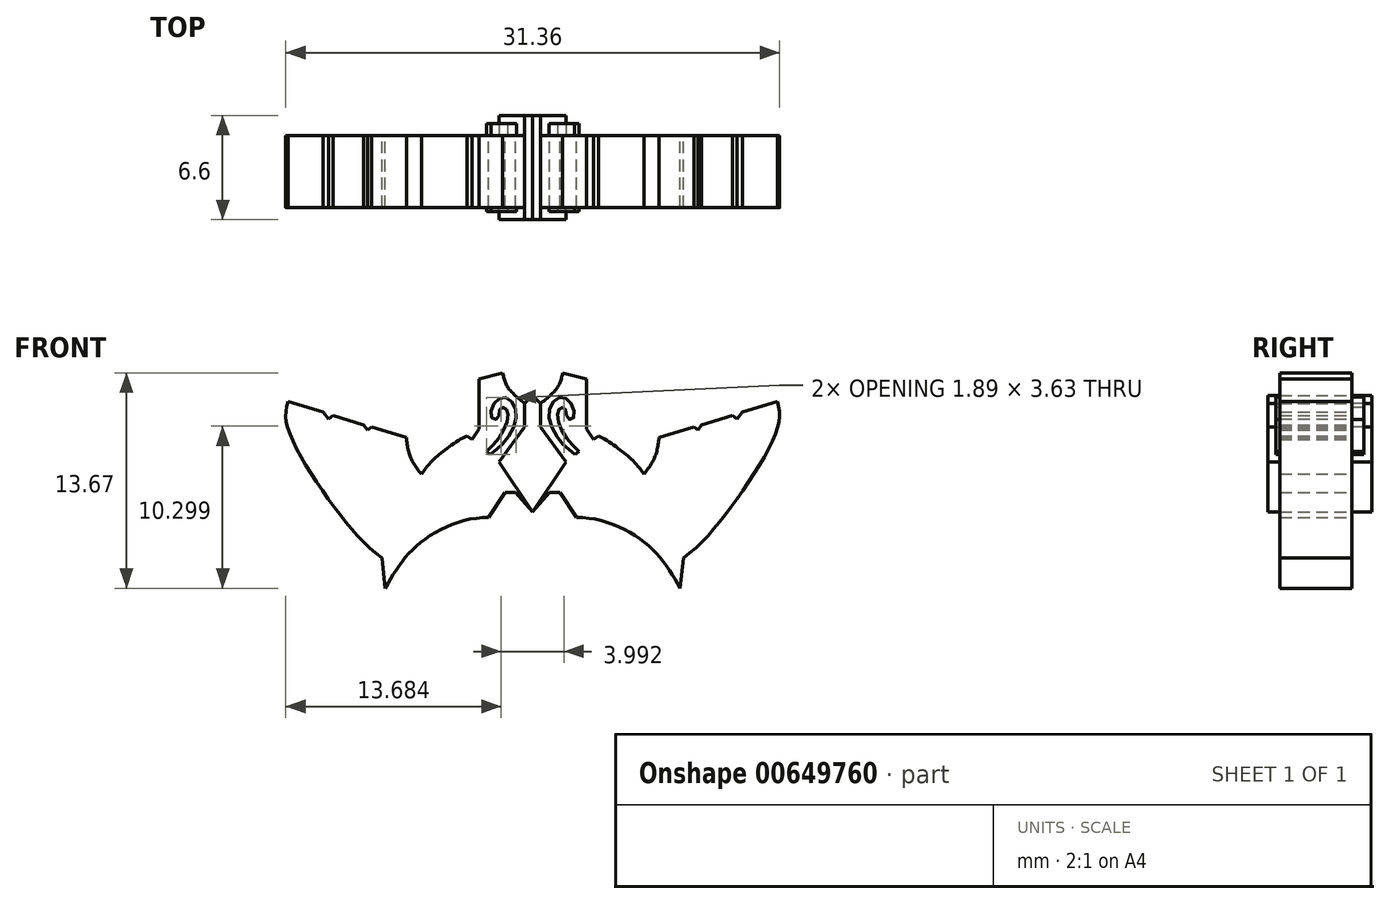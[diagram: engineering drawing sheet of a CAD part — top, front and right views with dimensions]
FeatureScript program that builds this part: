
annotation { "Feature Type Name" : "Feature", "Feature Type Description" : "" }
export const myFeature = defineFeature(function(context is Context, id is Id, definition is map)
    precondition{}
    {
        {
            var Q0;
            Q0=qCreatedBy(makeId("Front.planeOp"),FACE);
            var sketch = newSketch(context, id + "F0", { "sketchPlane" : qUnion([Q0])});
            skLineSegment(sketch, "E0", {"start": v(0, -28.32) * mm, "end": v(-0.51, -28.81) * mm});
            skFitSpline(sketch, "E1", {"points": [v(-0.51, -28.81) * mm, v(-1.6, -27.77) * mm, v(-1.9, -26.9) * mm], "startDerivative": vector(-2.3, 1.83) * mm, "endDerivative": vector(-0.4, 2.02) * mm});
            skLineSegment(sketch, "E2", {"start": v(-1.9, -26.9) * mm, "end": v(-3.41, -27.26) * mm});
            skLineSegment(sketch, "E3", {"start": v(-3.41, -27.26) * mm, "end": v(-3.41, -30.44) * mm});
            skLineSegment(sketch, "E4", {"start": v(-3.41, -30.44) * mm, "end": v(-3.86, -31.1) * mm});
            skLineSegment(sketch, "E5", {"start": v(-3.86, -31.1) * mm, "end": v(-4.17, -30.89) * mm});
            skFitSpline(sketch, "E6", {"points": [v(-4.17, -30.89) * mm, v(-5.74, -31.9) * mm, v(-7.06, -33.32) * mm], "startDerivative": vector(-2.94, -1.25) * mm, "endDerivative": vector(-3.05, -4.45) * mm});
            skFitSpline(sketch, "E7", {"points": [v(-7.06, -33.32) * mm, v(-7.77, -32.2) * mm, v(-8.02, -30.97) * mm], "startDerivative": vector(-1.62, 2.12) * mm, "endDerivative": vector(-0.3, 2.58) * mm});
            skLineSegment(sketch, "E8", {"start": v(-8.02, -30.97) * mm, "end": v(-10.24, -30.3) * mm});
            skLineSegment(sketch, "E9", {"start": v(-10.24, -30.3) * mm, "end": v(-10.5, -30.5) * mm});
            skLineSegment(sketch, "E10", {"start": v(-10.5, -30.5) * mm, "end": v(-10.73, -30.19) * mm});
            skLineSegment(sketch, "E11", {"start": v(-10.73, -30.19) * mm, "end": v(-12.7, -29.6) * mm});
            skLineSegment(sketch, "E12", {"start": v(-12.7, -29.6) * mm, "end": v(-12.97, -29.82) * mm});
            skLineSegment(sketch, "E13", {"start": v(-12.97, -29.82) * mm, "end": v(-13.32, -29.37) * mm});
            skLineSegment(sketch, "E14", {"start": v(-13.32, -29.37) * mm, "end": v(-15.54, -28.7) * mm});
            skFitSpline(sketch, "E15", {"points": [v(-15.54, -28.7) * mm, v(-15.54, -30.43) * mm, v(-12.88, -35.02) * mm, v(-9.57, -38.63) * mm], "startDerivative": vector(-2.17, -7.38) * mm, "endDerivative": vector(9.36, -6.6) * mm});
            skLineSegment(sketch, "E16", {"start": v(-9.57, -38.63) * mm, "end": v(-9.36, -40.56) * mm});
            skFitSpline(sketch, "E17", {"points": [v(-9.36, -40.56) * mm, v(-7.19, -37.7) * mm, v(-2.79, -36.08) * mm], "startDerivative": vector(3.82, 6.79) * mm, "endDerivative": vector(8.98, -0.25) * mm});
            skLineSegment(sketch, "E18", {"start": v(-2.79, -36.08) * mm, "end": v(-1.75, -34.48) * mm});
            skLineSegment(sketch, "E19", {"start": v(-1.75, -34.48) * mm, "end": v(-1.08, -34.48) * mm});
            skLineSegment(sketch, "E20", {"start": v(-1.08, -34.48) * mm, "end": v(0, -35.7) * mm});
            skLineSegment(sketch, "E21.MirrorCS", {"start": v(1.08, -34.48) * mm, "end": v(0, -35.7) * mm});
            skLineSegment(sketch, "E22.MirrorCS", {"start": v(1.75, -34.48) * mm, "end": v(1.08, -34.48) * mm});
            skLineSegment(sketch, "E23.MirrorCS", {"start": v(2.79, -36.08) * mm, "end": v(1.75, -34.48) * mm});
            skFitSpline(sketch, "E24.MirrorCS", {"points": [v(9.36, -40.56) * mm, v(7.19, -37.7) * mm, v(2.79, -36.08) * mm], "startDerivative": vector(-3.82, 6.79) * mm, "endDerivative": vector(-8.98, -0.25) * mm});
            skLineSegment(sketch, "E25.MirrorCS", {"start": v(9.57, -38.63) * mm, "end": v(9.36, -40.56) * mm});
            skFitSpline(sketch, "E26.MirrorCS", {"points": [v(15.54, -28.7) * mm, v(15.54, -30.43) * mm, v(12.88, -35.02) * mm, v(9.57, -38.63) * mm], "startDerivative": vector(2.17, -7.38) * mm, "endDerivative": vector(-9.36, -6.6) * mm});
            skLineSegment(sketch, "E27.MirrorCS", {"start": v(13.32, -29.37) * mm, "end": v(15.54, -28.7) * mm});
            skLineSegment(sketch, "E28.MirrorCS", {"start": v(12.97, -29.82) * mm, "end": v(13.32, -29.37) * mm});
            skLineSegment(sketch, "E29.MirrorCS", {"start": v(12.7, -29.6) * mm, "end": v(12.97, -29.82) * mm});
            skLineSegment(sketch, "E30.MirrorCS", {"start": v(10.73, -30.19) * mm, "end": v(12.7, -29.6) * mm});
            skLineSegment(sketch, "E31.MirrorCS", {"start": v(10.5, -30.5) * mm, "end": v(10.73, -30.19) * mm});
            skLineSegment(sketch, "E32.MirrorCS", {"start": v(10.24, -30.3) * mm, "end": v(10.5, -30.5) * mm});
            skLineSegment(sketch, "E33.MirrorCS", {"start": v(8.02, -30.97) * mm, "end": v(10.24, -30.3) * mm});
            skFitSpline(sketch, "E34.MirrorCS", {"points": [v(7.06, -33.32) * mm, v(7.77, -32.2) * mm, v(8.02, -30.97) * mm], "startDerivative": vector(1.62, 2.12) * mm, "endDerivative": vector(0.3, 2.58) * mm});
            skFitSpline(sketch, "E35.MirrorCS", {"points": [v(4.17, -30.89) * mm, v(5.74, -31.9) * mm, v(7.06, -33.32) * mm], "startDerivative": vector(2.94, -1.25) * mm, "endDerivative": vector(3.05, -4.45) * mm});
            skLineSegment(sketch, "E36.MirrorCS", {"start": v(3.86, -31.1) * mm, "end": v(4.17, -30.89) * mm});
            skLineSegment(sketch, "E37.MirrorCS", {"start": v(3.41, -30.44) * mm, "end": v(3.86, -31.1) * mm});
            skLineSegment(sketch, "E38.MirrorCS", {"start": v(3.41, -27.26) * mm, "end": v(3.41, -30.44) * mm});
            skLineSegment(sketch, "E39.MirrorCS", {"start": v(1.9, -26.9) * mm, "end": v(3.41, -27.26) * mm});
            skFitSpline(sketch, "E40.MirrorCS", {"points": [v(0.51, -28.81) * mm, v(1.6, -27.77) * mm, v(1.9, -26.9) * mm], "startDerivative": vector(2.3, 1.83) * mm, "endDerivative": vector(0.4, 2.02) * mm});
            skLineSegment(sketch, "E41.MirrorCS", {"start": v(0, -28.32) * mm, "end": v(0.51, -28.81) * mm});
            skSolve(sketch);
        }
        {
            var Q0;
            Q0=makeQuery(id+"F0.imprint","IMPRINT",FACE,{"disambiguationData":[TD([[makeQuery(id+"F0.imprint","IMPRINT",EDGE,{"derivedFrom":sQuery(id+"F0.wireOp",EDGE,"E0")}),1.0]])]});
            extrude(context, id + "F1", {"entities" : qUnion([Q0]), "depth" : 4.57 * mm, "offsetDistance" : 25.4 * mm});
        }
        {
            var Q0;
            Q0=makeQuery(id+"F1.opExtrude","CAP_FACE",FACE,{"disambiguationData":[OSD([sQuery(id+"F0.wireOp",EDGE,"E0"),sQuery(id+"F0.wireOp",EDGE,"E1"),sQuery(id+"F0.wireOp",EDGE,"E2"),sQuery(id+"F0.wireOp",EDGE,"E3"),sQuery(id+"F0.wireOp",EDGE,"E4"),sQuery(id+"F0.wireOp",EDGE,"E5"),sQuery(id+"F0.wireOp",EDGE,"E6"),sQuery(id+"F0.wireOp",EDGE,"E7"),sQuery(id+"F0.wireOp",EDGE,"E8"),sQuery(id+"F0.wireOp",EDGE,"E9"),sQuery(id+"F0.wireOp",EDGE,"E10"),sQuery(id+"F0.wireOp",EDGE,"E11"),sQuery(id+"F0.wireOp",EDGE,"E12"),sQuery(id+"F0.wireOp",EDGE,"E13"),sQuery(id+"F0.wireOp",EDGE,"E14"),sQuery(id+"F0.wireOp",EDGE,"E15"),sQuery(id+"F0.wireOp",EDGE,"E16"),sQuery(id+"F0.wireOp",EDGE,"E17"),sQuery(id+"F0.wireOp",EDGE,"E18"),sQuery(id+"F0.wireOp",EDGE,"E19"),sQuery(id+"F0.wireOp",EDGE,"E20"),sQuery(id+"F0.wireOp",EDGE,"E21.MirrorCS"),sQuery(id+"F0.wireOp",EDGE,"E22.MirrorCS"),sQuery(id+"F0.wireOp",EDGE,"E23.MirrorCS"),sQuery(id+"F0.wireOp",EDGE,"E24.MirrorCS"),sQuery(id+"F0.wireOp",EDGE,"E25.MirrorCS"),sQuery(id+"F0.wireOp",EDGE,"E26.MirrorCS"),sQuery(id+"F0.wireOp",EDGE,"E27.MirrorCS"),sQuery(id+"F0.wireOp",EDGE,"E28.MirrorCS"),sQuery(id+"F0.wireOp",EDGE,"E29.MirrorCS"),sQuery(id+"F0.wireOp",EDGE,"E30.MirrorCS"),sQuery(id+"F0.wireOp",EDGE,"E31.MirrorCS"),sQuery(id+"F0.wireOp",EDGE,"E32.MirrorCS"),sQuery(id+"F0.wireOp",EDGE,"E33.MirrorCS"),sQuery(id+"F0.wireOp",EDGE,"E34.MirrorCS"),sQuery(id+"F0.wireOp",EDGE,"E35.MirrorCS"),sQuery(id+"F0.wireOp",EDGE,"E36.MirrorCS"),sQuery(id+"F0.wireOp",EDGE,"E37.MirrorCS"),sQuery(id+"F0.wireOp",EDGE,"E38.MirrorCS"),sQuery(id+"F0.wireOp",EDGE,"E39.MirrorCS"),sQuery(id+"F0.wireOp",EDGE,"E40.MirrorCS"),sQuery(id+"F0.wireOp",EDGE,"E41.MirrorCS")])],"isStart":false});
            var sketch = newSketch(context, id + "F2", { "sketchPlane" : qUnion([Q0])});
            skLineSegment(sketch, "E42", {"start": v(0.51, -28.81) * mm, "end": v(0.51, -30.32) * mm});
            skLineSegment(sketch, "E43", {"start": v(0.51, -30.32) * mm, "end": v(2.13, -32.55) * mm});
            skLineSegment(sketch, "E44", {"start": v(2.13, -32.55) * mm, "end": v(0, -35.7) * mm});
            skLineSegment(sketch, "E45.MirrorCS", {"start": v(-0.51, -28.81) * mm, "end": v(-0.51, -30.32) * mm});
            skLineSegment(sketch, "E46.MirrorCS", {"start": v(-0.51, -30.32) * mm, "end": v(-2.13, -32.55) * mm});
            skLineSegment(sketch, "E47.MirrorCS", {"start": v(-2.13, -32.55) * mm, "end": v(0, -35.7) * mm});
            skLineSegment(sketch, "E48", {"start": v(-0.51, -28.81) * mm, "end": v(0, -28.32) * mm});
            skLineSegment(sketch, "E49", {"start": v(0, -28.32) * mm, "end": v(0.51, -28.81) * mm});
            skSolve(sketch);
        }
        {
            var Q0;
            Q0=makeQuery(id+"F2.imprint","IMPRINT",FACE,{"disambiguationData":[TD([[makeQuery(id+"F2.imprint","IMPRINT",EDGE,{"derivedFrom":sQuery(id+"F2.wireOp",EDGE,"E42")}),-1.0]])]});
            extrude(context, id + "F3", {"entities" : qUnion([Q0]), "operationType" : NewBodyOperationType.ADD, "depth" : 0.76 * mm, "offsetDistance" : 25.4 * mm});
        }
        {
            var Q0;
            {var subQ0=sQuery(id+"F0.wireOp",EDGE,"E40.MirrorCS");var subQ1=sQuery(id+"F0.wireOp",EDGE,"E39.MirrorCS");var subQ2=sQuery(id+"F0.wireOp",EDGE,"E38.MirrorCS");var subQ3=sQuery(id+"F0.wireOp",EDGE,"E37.MirrorCS");var subQ4=sQuery(id+"F0.wireOp",EDGE,"E36.MirrorCS");var subQ5=sQuery(id+"F0.wireOp",EDGE,"E35.MirrorCS");var subQ6=sQuery(id+"F0.wireOp",EDGE,"E34.MirrorCS");var subQ7=sQuery(id+"F0.wireOp",EDGE,"E33.MirrorCS");var subQ8=sQuery(id+"F0.wireOp",EDGE,"E32.MirrorCS");var subQ9=sQuery(id+"F0.wireOp",EDGE,"E31.MirrorCS");var subQ10=sQuery(id+"F0.wireOp",EDGE,"E30.MirrorCS");var subQ11=sQuery(id+"F0.wireOp",EDGE,"E29.MirrorCS");var subQ12=sQuery(id+"F0.wireOp",EDGE,"E22.MirrorCS");var subQ13=sQuery(id+"F0.wireOp",EDGE,"E21.MirrorCS");var subQ14=sQuery(id+"F0.wireOp",EDGE,"E20");var subQ15=sQuery(id+"F0.wireOp",EDGE,"E41.MirrorCS");var subQ16=sQuery(id+"F0.wireOp",EDGE,"E28.MirrorCS");var subQ17=sQuery(id+"F0.wireOp",EDGE,"E27.MirrorCS");var subQ18=sQuery(id+"F0.wireOp",EDGE,"E26.MirrorCS");var subQ19=sQuery(id+"F0.wireOp",EDGE,"E25.MirrorCS");var subQ20=sQuery(id+"F0.wireOp",EDGE,"E24.MirrorCS");var subQ21=sQuery(id+"F0.wireOp",EDGE,"E23.MirrorCS");var subQ22=makeQuery(id+"F1.opExtrude","CAP_FACE",FACE,{"disambiguationData":[OSD([sQuery(id+"F0.wireOp",EDGE,"E0"),sQuery(id+"F0.wireOp",EDGE,"E1"),sQuery(id+"F0.wireOp",EDGE,"E2"),sQuery(id+"F0.wireOp",EDGE,"E3"),sQuery(id+"F0.wireOp",EDGE,"E4"),sQuery(id+"F0.wireOp",EDGE,"E5"),sQuery(id+"F0.wireOp",EDGE,"E6"),sQuery(id+"F0.wireOp",EDGE,"E7"),sQuery(id+"F0.wireOp",EDGE,"E8"),sQuery(id+"F0.wireOp",EDGE,"E9"),sQuery(id+"F0.wireOp",EDGE,"E10"),sQuery(id+"F0.wireOp",EDGE,"E11"),sQuery(id+"F0.wireOp",EDGE,"E12"),sQuery(id+"F0.wireOp",EDGE,"E13"),sQuery(id+"F0.wireOp",EDGE,"E14"),sQuery(id+"F0.wireOp",EDGE,"E15"),sQuery(id+"F0.wireOp",EDGE,"E16"),sQuery(id+"F0.wireOp",EDGE,"E17"),sQuery(id+"F0.wireOp",EDGE,"E18"),sQuery(id+"F0.wireOp",EDGE,"E19"),subQ14,subQ13,subQ12,subQ21,subQ20,subQ19,subQ18,subQ17,subQ16,subQ11,subQ10,subQ9,subQ8,subQ7,subQ6,subQ5,subQ4,subQ3,subQ2,subQ1,subQ0,subQ15])],"isStart":false});Q0=makeQuery(id+"F3.boolean.opBoolean","SPLIT",FACE,{"disambiguationData":[TD([makeQuery(id+"F1.opExtrude","SWEPT_FACE",FACE,{"disambiguationData":[OSD([subQ12])]})])],"derivedFrom":subQ22});}
            var sketch = newSketch(context, id + "F4", { "sketchPlane" : qUnion([Q0])});
            skLineSegment(sketch, "E50", {"start": v(3.86, -31.1) * mm, "end": v(2.13, -32.55) * mm});
            skFitSpline(sketch, "E51", {"points": [v(2.7, -32.08) * mm, v(1.69, -31.14) * mm, v(1.04, -29.4) * mm, v(1.69, -28.45) * mm, v(2.43, -28.81) * mm, v(2.59, -29.75) * mm, v(2.2, -29.76) * mm, v(2.08, -29.16) * mm, v(1.8, -29.1) * mm, v(1.59, -29.44) * mm, v(1.89, -30.62) * mm, v(2.94, -31.88) * mm], "startDerivative": vector(-9.27, 7) * mm, "endDerivative": vector(9.7, -9.61) * mm});
            skFitSpline(sketch, "E52.MirrorCS", {"points": [v(-2.7, -32.08) * mm, v(-1.69, -31.14) * mm, v(-1.04, -29.4) * mm, v(-1.69, -28.45) * mm, v(-2.43, -28.81) * mm, v(-2.59, -29.75) * mm, v(-2.2, -29.76) * mm, v(-2.08, -29.16) * mm, v(-1.8, -29.1) * mm, v(-1.59, -29.44) * mm, v(-1.89, -30.62) * mm, v(-2.94, -31.88) * mm], "startDerivative": vector(9.27, 7) * mm, "endDerivative": vector(-9.7, -9.61) * mm});
            skLineSegment(sketch, "E53.MirrorCS", {"start": v(-3.86, -31.1) * mm, "end": v(-2.13, -32.55) * mm});
            skSolve(sketch);
        }
        {
            var Q0;
            {var subQ0=sQuery(id+"F4.wireOp",EDGE,"E52.MirrorCS");Q0=makeQuery(id+"F4.imprint","IMPRINT",FACE,{"disambiguationData":[TD([[makeQuery(id+"F4.imprint","IMPRINT",EDGE,{"derivedFrom":subQ0}),1.0]])]});}
            var Q1;
            {var subQ0=sQuery(id+"F4.wireOp",EDGE,"E51");Q1=makeQuery(id+"F4.imprint","IMPRINT",FACE,{"disambiguationData":[TD([[makeQuery(id+"F4.imprint","IMPRINT",EDGE,{"derivedFrom":subQ0}),-1.0]])]});}
            extrude(context, id + "F5", {"entities" : qUnion([Q0, Q1]), "operationType" : NewBodyOperationType.ADD, "depth" : 0.25 * mm, "offsetDistance" : 25.4 * mm});
        }
        {
            var Q0;
            Q0 = qSketchRegion(id + "F2", true);
            extrude(context, id + "F6", {"entities" : qUnion([Q0]), "operationType" : NewBodyOperationType.ADD, "oppositeDirection" : true, "depth" : 5.84 * mm, "offsetDistance" : 25.4 * mm});
        }
        {
            var Q0;
            Q0=makeQuery(id+"F5.opExtrude","CAP_FACE",FACE,{"disambiguationData":[OSD([sQuery(id+"F4.wireOp",EDGE,"E50"),sQuery(id+"F4.wireOp",EDGE,"E51")])],"isStart":false});
            var Q1;
            Q1=makeQuery(id+"F5.opExtrude","CAP_FACE",FACE,{"disambiguationData":[OSD([sQuery(id+"F4.wireOp",EDGE,"E52.MirrorCS"),sQuery(id+"F4.wireOp",EDGE,"E53.MirrorCS")])],"isStart":false});
            extrude(context, id + "F7", {"entities" : qUnion([Q0, Q1]), "operationType" : NewBodyOperationType.ADD, "oppositeDirection" : true, "depth" : 5.6 * mm, "offsetDistance" : 25.4 * mm});
        }
    });
